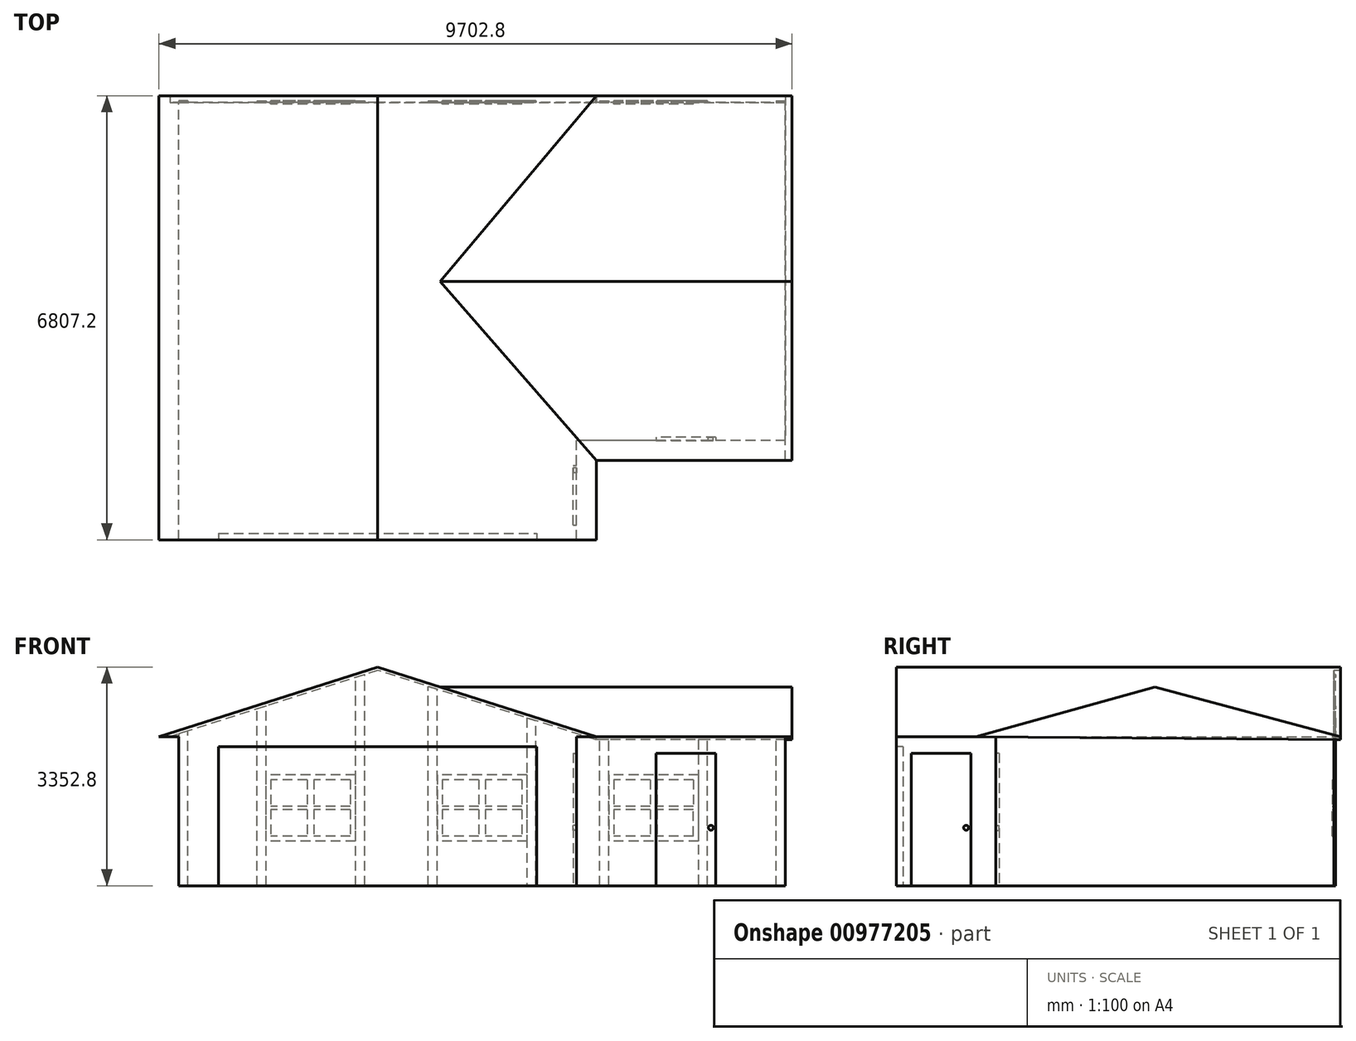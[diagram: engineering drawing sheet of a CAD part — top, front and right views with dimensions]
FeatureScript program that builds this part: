
annotation { "Feature Type Name" : "Feature", "Feature Type Description" : "" }
export const myFeature = defineFeature(function(context is Context, id is Id, definition is map)
    precondition{}
    {
        {
            var Q0;
            Q0=qCreatedBy(makeId("Front.planeOp"),FACE);
            var sketch = newSketch(context, id + "F0", { "sketchPlane" : qUnion([Q0])});
            skLineSegment(sketch, "E0", {"start": v(334.67, 1660.37) * mm, "end": v(-3018.13, 593.57) * mm});
            skLineSegment(sketch, "E1", {"start": v(-3018.13, 593.57) * mm, "end": v(-2713.33, 593.57) * mm});
            skLineSegment(sketch, "E2", {"start": v(-2713.33, 593.57) * mm, "end": v(-2713.33, -1692.43) * mm});
            skLineSegment(sketch, "E3", {"start": v(-2713.33, -1692.43) * mm, "end": v(3382.67, -1692.43) * mm});
            skLineSegment(sketch, "E4", {"start": v(3382.67, -1692.43) * mm, "end": v(3382.67, 593.57) * mm});
            skLineSegment(sketch, "E5", {"start": v(3382.67, 593.57) * mm, "end": v(3687.47, 593.57) * mm});
            skLineSegment(sketch, "E6", {"start": v(3687.47, 593.57) * mm, "end": v(334.67, 1660.37) * mm});
            skSolve(sketch);
        }
        {
            var Q0;
            Q0 = qSketchRegion(id + "F0", true);
            extrude(context, id + "F1", {"entities" : qUnion([Q0]), "depth" : 22 * 304.8 * mm, "offsetDistance" : 25.4 * mm});
        }
        {
            var Q0;
            Q0=makeQuery(id+"F1.opExtrude","CAP_FACE",FACE,{"disambiguationData":[OSD([sQuery(id+"F0.wireOp",EDGE,"E0"),sQuery(id+"F0.wireOp",EDGE,"E1"),sQuery(id+"F0.wireOp",EDGE,"E2"),sQuery(id+"F0.wireOp",EDGE,"E3"),sQuery(id+"F0.wireOp",EDGE,"E4"),sQuery(id+"F0.wireOp",EDGE,"E5"),sQuery(id+"F0.wireOp",EDGE,"E6")])],"isStart":false});
            var sketch = newSketch(context, id + "F2", { "sketchPlane" : qUnion([Q0])});
            skLineSegment(sketch, "E7.bottom", {"start": v(-2103.73, 441.17) * mm, "end": v(2773.07, 441.17) * mm});
            skLineSegment(sketch, "E7.top", {"start": v(-2103.73, -1692.43) * mm, "end": v(2773.07, -1692.43) * mm});
            skLineSegment(sketch, "E7.left", {"start": v(-2103.73, 441.17) * mm, "end": v(-2103.73, -1692.43) * mm});
            skLineSegment(sketch, "E7.right", {"start": v(2773.07, 441.17) * mm, "end": v(2773.07, -1692.43) * mm});
            skSolve(sketch);
        }
        {
            var Q0;
            Q0 = qSketchRegion(id + "F2", true);
            extrude(context, id + "F3", {"entities" : qUnion([Q0]), "operationType" : NewBodyOperationType.REMOVE, "oppositeDirection" : true, "depth" : 101.6 * mm, "offsetDistance" : 25.4 * mm});
        }
        {
            var Q0;
            Q0=makeQuery(id+"F1.opExtrude","SWEPT_FACE",FACE,{"disambiguationData":[OSD([sQuery(id+"F0.wireOp",EDGE,"E4")])]});
            var sketch = newSketch(context, id + "F4", { "sketchPlane" : qUnion([Q0])});
            skLineSegment(sketch, "E8.bottom", {"start": v(-6477, 339.57) * mm, "end": v(-5562.6, 339.57) * mm});
            skLineSegment(sketch, "E8.top", {"start": v(-6477, -1692.43) * mm, "end": v(-5562.6, -1692.43) * mm});
            skLineSegment(sketch, "E8.left", {"start": v(-6477, 339.57) * mm, "end": v(-6477, -1692.43) * mm});
            skLineSegment(sketch, "E8.right", {"start": v(-5562.6, 339.57) * mm, "end": v(-5562.6, -1692.43) * mm});
            skSolve(sketch);
        }
        {
            var Q0;
            Q0 = qSketchRegion(id + "F4", true);
            extrude(context, id + "F5", {"entities" : qUnion([Q0]), "operationType" : NewBodyOperationType.REMOVE, "oppositeDirection" : true, "depth" : 50.8 * mm, "offsetDistance" : 25.4 * mm});
        }
        {
            var Q0;
            Q0=makeQuery(id+"F1.opExtrude","SWEPT_FACE",FACE,{"disambiguationData":[OSD([sQuery(id+"F0.wireOp",EDGE,"E4")])]});
            var sketch = newSketch(context, id + "F6", { "sketchPlane" : qUnion([Q0])});
            skLineSegment(sketch, "E9", {"start": v(-5181.6, -1692.43) * mm, "end": v(-5181.6, 593.57) * mm});
            skLineSegment(sketch, "E10", {"start": v(-5181.6, 593.57) * mm, "end": v(-5486.4, 593.57) * mm});
            skLineSegment(sketch, "E11", {"start": v(-5486.4, 593.57) * mm, "end": v(-2743.2, 1355.57) * mm});
            skLineSegment(sketch, "E12", {"start": v(0, 593.57) * mm, "end": v(0, -1692.43) * mm});
            skLineSegment(sketch, "E13", {"start": v(0, -1692.43) * mm, "end": v(-5181.6, -1692.43) * mm});
            skLineSegment(sketch, "E14", {"start": v(-2743.2, 1355.57) * mm, "end": v(0, 593.57) * mm});
            skSolve(sketch);
        }
        {
            var Q0;
            Q0 = qSketchRegion(id + "F6", true);
            var Q1;
            Q1=makeQuery(id+"F1.opExtrude","SWEPT_FACE",FACE,{"disambiguationData":[OSD([sQuery(id+"F0.wireOp",EDGE,"E6")])]});
            extrude(context, id + "F7", {"entities" : qUnion([Q0]), "operationType" : NewBodyOperationType.ADD, "depth" : 3200.4 * mm, "offsetDistance" : 25.4 * mm, "hasSecondDirection" : true, "secondDirectionBound" : SecondDirectionBoundingType.UP_TO_NEXT, "secondDirectionOppositeDirection" : true, "secondDirectionDepth" : 25.4 * mm, "secondDirectionBoundEntityFace" : qUnion([Q1])});
        }
        {
            var Q0;
            Q0=makeQuery(id+"F7.opExtrude","SWEPT_FACE",FACE,{"disambiguationData":[OSD([sQuery(id+"F6.wireOp",EDGE,"E9")])]});
            var sketch = newSketch(context, id + "F8", { "sketchPlane" : qUnion([Q0])});
            skLineSegment(sketch, "E15.bottom", {"start": v(4601.87, 339.57) * mm, "end": v(5516.27, 339.57) * mm});
            skLineSegment(sketch, "E15.top", {"start": v(4601.87, -1692.43) * mm, "end": v(5516.27, -1692.43) * mm});
            skLineSegment(sketch, "E15.left", {"start": v(4601.87, 339.57) * mm, "end": v(4601.87, -1692.43) * mm});
            skLineSegment(sketch, "E15.right", {"start": v(5516.27, 339.57) * mm, "end": v(5516.27, -1692.43) * mm});
            skSolve(sketch);
        }
        {
            var Q0;
            Q0 = qSketchRegion(id + "F8", true);
            extrude(context, id + "F9", {"entities" : qUnion([Q0]), "operationType" : NewBodyOperationType.REMOVE, "oppositeDirection" : true, "depth" : 50.8 * mm, "offsetDistance" : 25.4 * mm});
        }
        {
            var Q0;
            Q0=makeQuery(id+"F7.boolean.opBoolean","MERGE",FACE,{"derivedFrom":[makeQuery(id+"F1.opExtrude","CAP_FACE",FACE,{"disambiguationData":[OSD([sQuery(id+"F0.wireOp",EDGE,"E0"),sQuery(id+"F0.wireOp",EDGE,"E1"),sQuery(id+"F0.wireOp",EDGE,"E2"),sQuery(id+"F0.wireOp",EDGE,"E3"),sQuery(id+"F0.wireOp",EDGE,"E4"),sQuery(id+"F0.wireOp",EDGE,"E5"),sQuery(id+"F0.wireOp",EDGE,"E6")])],"isStart":true}),makeQuery(id+"F7.opExtrude","SWEPT_FACE",FACE,{"disambiguationData":[OSD([sQuery(id+"F6.wireOp",EDGE,"E12")])]})]});
            var sketch = newSketch(context, id + "F10", { "sketchPlane" : qUnion([Q0])});
            skLineSegment(sketch, "E16.bottom", {"start": v(-5173.37, -66.83) * mm, "end": v(-4614.57, -66.83) * mm});
            skLineSegment(sketch, "E16.top", {"start": v(-5173.37, -930.43) * mm, "end": v(-4614.57, -930.43) * mm});
            skLineSegment(sketch, "E16.left", {"start": v(-5173.37, -66.83) * mm, "end": v(-5173.37, -473.23) * mm});
            skLineSegment(sketch, "E16.right", {"start": v(-4614.57, -66.83) * mm, "end": v(-4614.57, -473.23) * mm});
            skLineSegment(sketch, "E17.top", {"start": v(-4512.97, -930.43) * mm, "end": v(-3954.17, -930.43) * mm});
            skLineSegment(sketch, "E17.left", {"start": v(-4512.97, -66.83) * mm, "end": v(-4512.97, -473.23) * mm});
            skLineSegment(sketch, "E17.right", {"start": v(-3954.17, -66.83) * mm, "end": v(-3954.17, -473.23) * mm});
            skLineSegment(sketch, "E18.top", {"start": v(-2544.47, -930.43) * mm, "end": v(-1985.67, -930.43) * mm});
            skLineSegment(sketch, "E18.left", {"start": v(-2544.47, -66.83) * mm, "end": v(-2544.47, -473.23) * mm});
            skLineSegment(sketch, "E18.right", {"start": v(-1985.67, -66.83) * mm, "end": v(-1985.67, -473.23) * mm});
            skLineSegment(sketch, "E19.top", {"start": v(-1884.07, -930.43) * mm, "end": v(-1325.27, -930.43) * mm});
            skLineSegment(sketch, "E19.left", {"start": v(-1884.07, -66.83) * mm, "end": v(-1884.07, -473.23) * mm});
            skLineSegment(sketch, "E19.right", {"start": v(-1325.27, -66.83) * mm, "end": v(-1325.27, -473.23) * mm});
            skLineSegment(sketch, "E20.top", {"start": v(84.43, -930.43) * mm, "end": v(643.23, -930.43) * mm});
            skLineSegment(sketch, "E20.left", {"start": v(84.43, -66.83) * mm, "end": v(84.43, -473.23) * mm});
            skLineSegment(sketch, "E20.right", {"start": v(643.23, -66.83) * mm, "end": v(643.23, -473.23) * mm});
            skLineSegment(sketch, "E21.top", {"start": v(744.83, -930.43) * mm, "end": v(1303.63, -930.43) * mm});
            skLineSegment(sketch, "E21.left", {"start": v(744.83, -66.83) * mm, "end": v(744.83, -473.23) * mm});
            skLineSegment(sketch, "E21.right", {"start": v(1303.63, -66.83) * mm, "end": v(1303.63, -473.23) * mm});
            skLineSegment(sketch, "E22", {"start": v(-4512.97, -524.03) * mm, "end": v(-3954.17, -524.03) * mm});
            skLineSegment(sketch, "E23", {"start": v(-2544.47, -524.03) * mm, "end": v(-1985.67, -524.03) * mm});
            skLineSegment(sketch, "E24", {"start": v(-1884.07, -524.03) * mm, "end": v(-1325.27, -524.03) * mm});
            skLineSegment(sketch, "E25", {"start": v(84.43, -524.03) * mm, "end": v(643.23, -524.03) * mm});
            skLineSegment(sketch, "E26", {"start": v(744.83, -524.03) * mm, "end": v(1303.63, -524.03) * mm});
            skLineSegment(sketch, "E27", {"start": v(-5173.37, -473.23) * mm, "end": v(-4614.57, -473.23) * mm});
            skLineSegment(sketch, "E28", {"start": v(-4512.97, -473.23) * mm, "end": v(-3954.17, -473.23) * mm});
            skLineSegment(sketch, "E29", {"start": v(-2544.47, -473.23) * mm, "end": v(-1985.67, -473.23) * mm});
            skLineSegment(sketch, "E30", {"start": v(-1884.07, -473.23) * mm, "end": v(-1325.27, -473.23) * mm});
            skLineSegment(sketch, "E31", {"start": v(84.43, -473.23) * mm, "end": v(643.23, -473.23) * mm});
            skLineSegment(sketch, "E32", {"start": v(744.83, -473.23) * mm, "end": v(1303.63, -473.23) * mm});
            skLineSegment(sketch, "E33.trimOffspring", {"start": v(-3954.17, -524.03) * mm, "end": v(-3954.17, -930.43) * mm});
            skLineSegment(sketch, "E34.trimOffspring", {"start": v(-4614.57, -524.03) * mm, "end": v(-4614.57, -930.43) * mm});
            skLineSegment(sketch, "E35.trimOffspring", {"start": v(-4512.97, -524.03) * mm, "end": v(-4512.97, -930.43) * mm});
            skLineSegment(sketch, "E36.trimOffspring", {"start": v(-2544.47, -524.03) * mm, "end": v(-2544.47, -930.43) * mm});
            skLineSegment(sketch, "E37.trimOffspring", {"start": v(-1884.07, -524.03) * mm, "end": v(-1884.07, -930.43) * mm});
            skLineSegment(sketch, "E38.trimOffspring", {"start": v(-1325.27, -524.03) * mm, "end": v(-1325.27, -930.43) * mm});
            skLineSegment(sketch, "E39.trimOffspring", {"start": v(-1985.67, -524.03) * mm, "end": v(-1985.67, -930.43) * mm});
            skLineSegment(sketch, "E40.trimOffspring", {"start": v(84.43, -524.03) * mm, "end": v(84.43, -930.43) * mm});
            skLineSegment(sketch, "E41.trimOffspring", {"start": v(643.23, -524.03) * mm, "end": v(643.23, -930.43) * mm});
            skLineSegment(sketch, "E42.trimOffspring", {"start": v(744.83, -524.03) * mm, "end": v(744.83, -930.43) * mm});
            skLineSegment(sketch, "E43.trimOffspring", {"start": v(1303.63, -524.03) * mm, "end": v(1303.63, -930.43) * mm});
            skLineSegment(sketch, "E44", {"start": v(-5173.37, -930.43) * mm, "end": v(-5173.37, -524.03) * mm});
            skLineSegment(sketch, "E45", {"start": v(-5173.37, -524.03) * mm, "end": v(-4614.57, -524.03) * mm});
            skLineSegment(sketch, "E46", {"start": v(-4512.97, -66.83) * mm, "end": v(-3954.17, -66.83) * mm});
            skLineSegment(sketch, "E47.trimOffspring", {"start": v(-2544.47, -66.83) * mm, "end": v(-1985.67, -66.83) * mm});
            skLineSegment(sketch, "E48.trimOffspring", {"start": v(84.43, -66.83) * mm, "end": v(643.23, -66.83) * mm});
            skLineSegment(sketch, "E49.trimOffspring", {"start": v(744.83, -66.83) * mm, "end": v(1303.63, -66.83) * mm});
            skLineSegment(sketch, "E50.trimOffspring", {"start": v(-1884.07, -66.83) * mm, "end": v(-1325.27, -66.83) * mm});
            skSolve(sketch);
        }
        {
            var Q0;
            Q0 = qSketchRegion(id + "F10", true);
            extrude(context, id + "F11", {"entities" : qUnion([Q0]), "operationType" : NewBodyOperationType.REMOVE, "oppositeDirection" : true, "depth" : 25.4 * mm, "offsetDistance" : 25.4 * mm});
        }
        {
            var Q0;
            Q0=makeQuery(id+"F7.boolean.opBoolean","MERGE",FACE,{"derivedFrom":[makeQuery(id+"F1.opExtrude","CAP_FACE",FACE,{"disambiguationData":[OSD([sQuery(id+"F0.wireOp",EDGE,"E0"),sQuery(id+"F0.wireOp",EDGE,"E1"),sQuery(id+"F0.wireOp",EDGE,"E2"),sQuery(id+"F0.wireOp",EDGE,"E3"),sQuery(id+"F0.wireOp",EDGE,"E4"),sQuery(id+"F0.wireOp",EDGE,"E5"),sQuery(id+"F0.wireOp",EDGE,"E6")])],"isStart":true}),makeQuery(id+"F7.opExtrude","SWEPT_FACE",FACE,{"disambiguationData":[OSD([sQuery(id+"F6.wireOp",EDGE,"E12")])]})]});
            var sketch = newSketch(context, id + "F12", { "sketchPlane" : qUnion([Q0])});
            skLineSegment(sketch, "E51.bottom", {"start": v(-5249.57, 9.37) * mm, "end": v(-3877.97, 9.37) * mm});
            skLineSegment(sketch, "E51.top", {"start": v(-5249.57, -1006.63) * mm, "end": v(-3877.97, -1006.63) * mm});
            skLineSegment(sketch, "E51.left", {"start": v(-5249.57, 9.37) * mm, "end": v(-5249.57, -1006.63) * mm});
            skLineSegment(sketch, "E51.right", {"start": v(-3877.97, 9.37) * mm, "end": v(-3877.97, -1006.63) * mm});
            skLineSegment(sketch, "E52.bottom", {"start": v(-2620.67, 9.37) * mm, "end": v(-1249.07, 9.37) * mm});
            skLineSegment(sketch, "E52.top", {"start": v(-2620.67, -1006.63) * mm, "end": v(-1249.07, -1006.63) * mm});
            skLineSegment(sketch, "E52.left", {"start": v(-2620.67, 9.37) * mm, "end": v(-2620.67, -1006.63) * mm});
            skLineSegment(sketch, "E52.right", {"start": v(-1249.07, 9.37) * mm, "end": v(-1249.07, -1006.63) * mm});
            skLineSegment(sketch, "E53.bottom", {"start": v(8.23, 9.37) * mm, "end": v(1379.83, 9.37) * mm});
            skLineSegment(sketch, "E53.top", {"start": v(8.23, -1006.63) * mm, "end": v(1379.83, -1006.63) * mm});
            skLineSegment(sketch, "E53.left", {"start": v(8.23, 9.37) * mm, "end": v(8.23, -1006.63) * mm});
            skLineSegment(sketch, "E53.right", {"start": v(1379.83, 9.37) * mm, "end": v(1379.83, -1006.63) * mm});
            skLineSegment(sketch, "E54.bottom", {"start": v(-5173.37, -66.83) * mm, "end": v(-4614.57, -66.83) * mm});
            skLineSegment(sketch, "E54.top", {"start": v(-5173.37, -473.23) * mm, "end": v(-4614.57, -473.23) * mm});
            skLineSegment(sketch, "E54.left", {"start": v(-5173.37, -66.83) * mm, "end": v(-5173.37, -473.23) * mm});
            skLineSegment(sketch, "E54.right", {"start": v(-4614.57, -66.83) * mm, "end": v(-4614.57, -473.23) * mm});
            skLineSegment(sketch, "E55.bottom", {"start": v(-4512.97, -66.83) * mm, "end": v(-3954.17, -66.83) * mm});
            skLineSegment(sketch, "E55.top", {"start": v(-4512.97, -473.23) * mm, "end": v(-3954.17, -473.23) * mm});
            skLineSegment(sketch, "E55.left", {"start": v(-4512.97, -66.83) * mm, "end": v(-4512.97, -473.23) * mm});
            skLineSegment(sketch, "E55.right", {"start": v(-3954.17, -66.83) * mm, "end": v(-3954.17, -473.23) * mm});
            skLineSegment(sketch, "E56.bottom", {"start": v(-4512.97, -524.03) * mm, "end": v(-3954.17, -524.03) * mm});
            skLineSegment(sketch, "E56.top", {"start": v(-4512.97, -930.43) * mm, "end": v(-3954.17, -930.43) * mm});
            skLineSegment(sketch, "E56.left", {"start": v(-4512.97, -524.03) * mm, "end": v(-4512.97, -930.43) * mm});
            skLineSegment(sketch, "E56.right", {"start": v(-3954.17, -524.03) * mm, "end": v(-3954.17, -930.43) * mm});
            skLineSegment(sketch, "E57.bottom", {"start": v(-5173.37, -524.03) * mm, "end": v(-4614.57, -524.03) * mm});
            skLineSegment(sketch, "E57.top", {"start": v(-5173.37, -930.43) * mm, "end": v(-4614.57, -930.43) * mm});
            skLineSegment(sketch, "E57.left", {"start": v(-5173.37, -524.03) * mm, "end": v(-5173.37, -930.43) * mm});
            skLineSegment(sketch, "E57.right", {"start": v(-4614.57, -524.03) * mm, "end": v(-4614.57, -930.43) * mm});
            skLineSegment(sketch, "E58.bottom", {"start": v(-2544.47, -66.83) * mm, "end": v(-1985.67, -66.83) * mm});
            skLineSegment(sketch, "E58.top", {"start": v(-2544.47, -473.23) * mm, "end": v(-1985.67, -473.23) * mm});
            skLineSegment(sketch, "E58.left", {"start": v(-2544.47, -66.83) * mm, "end": v(-2544.47, -473.23) * mm});
            skLineSegment(sketch, "E58.right", {"start": v(-1985.67, -66.83) * mm, "end": v(-1985.67, -473.23) * mm});
            skLineSegment(sketch, "E59.bottom", {"start": v(-1884.07, -66.83) * mm, "end": v(-1325.27, -66.83) * mm});
            skLineSegment(sketch, "E59.top", {"start": v(-1884.07, -473.23) * mm, "end": v(-1325.27, -473.23) * mm});
            skLineSegment(sketch, "E59.left", {"start": v(-1884.07, -66.83) * mm, "end": v(-1884.07, -473.23) * mm});
            skLineSegment(sketch, "E59.right", {"start": v(-1325.27, -66.83) * mm, "end": v(-1325.27, -473.23) * mm});
            skLineSegment(sketch, "E60.bottom", {"start": v(84.43, -66.83) * mm, "end": v(643.23, -66.83) * mm});
            skLineSegment(sketch, "E60.top", {"start": v(84.43, -473.23) * mm, "end": v(643.23, -473.23) * mm});
            skLineSegment(sketch, "E60.left", {"start": v(84.43, -66.83) * mm, "end": v(84.43, -473.23) * mm});
            skLineSegment(sketch, "E60.right", {"start": v(643.23, -66.83) * mm, "end": v(643.23, -473.23) * mm});
            skLineSegment(sketch, "E61.bottom", {"start": v(744.83, -66.83) * mm, "end": v(1303.63, -66.83) * mm});
            skLineSegment(sketch, "E61.top", {"start": v(744.83, -473.23) * mm, "end": v(1303.63, -473.23) * mm});
            skLineSegment(sketch, "E61.left", {"start": v(744.83, -66.83) * mm, "end": v(744.83, -473.23) * mm});
            skLineSegment(sketch, "E61.right", {"start": v(1303.63, -66.83) * mm, "end": v(1303.63, -473.23) * mm});
            skLineSegment(sketch, "E62.bottom", {"start": v(744.83, -524.03) * mm, "end": v(1303.63, -524.03) * mm});
            skLineSegment(sketch, "E62.top", {"start": v(744.83, -930.43) * mm, "end": v(1303.63, -930.43) * mm});
            skLineSegment(sketch, "E62.left", {"start": v(744.83, -524.03) * mm, "end": v(744.83, -930.43) * mm});
            skLineSegment(sketch, "E62.right", {"start": v(1303.63, -524.03) * mm, "end": v(1303.63, -930.43) * mm});
            skLineSegment(sketch, "E63.bottom", {"start": v(-1884.07, -524.03) * mm, "end": v(-1325.27, -524.03) * mm});
            skLineSegment(sketch, "E63.top", {"start": v(-1884.07, -930.43) * mm, "end": v(-1325.27, -930.43) * mm});
            skLineSegment(sketch, "E63.left", {"start": v(-1884.07, -524.03) * mm, "end": v(-1884.07, -930.43) * mm});
            skLineSegment(sketch, "E63.right", {"start": v(-1325.27, -524.03) * mm, "end": v(-1325.27, -930.43) * mm});
            skLineSegment(sketch, "E64.bottom", {"start": v(-2544.47, -524.03) * mm, "end": v(-1985.67, -524.03) * mm});
            skLineSegment(sketch, "E64.top", {"start": v(-2544.47, -930.43) * mm, "end": v(-1985.67, -930.43) * mm});
            skLineSegment(sketch, "E64.left", {"start": v(-2544.47, -524.03) * mm, "end": v(-2544.47, -930.43) * mm});
            skLineSegment(sketch, "E64.right", {"start": v(-1985.67, -524.03) * mm, "end": v(-1985.67, -930.43) * mm});
            skLineSegment(sketch, "E65.bottom", {"start": v(84.43, -524.03) * mm, "end": v(643.23, -524.03) * mm});
            skLineSegment(sketch, "E65.top", {"start": v(84.43, -930.43) * mm, "end": v(643.23, -930.43) * mm});
            skLineSegment(sketch, "E65.left", {"start": v(84.43, -524.03) * mm, "end": v(84.43, -930.43) * mm});
            skLineSegment(sketch, "E65.right", {"start": v(643.23, -524.03) * mm, "end": v(643.23, -930.43) * mm});
            skSolve(sketch);
        }
        {
            var Q0;
            Q0=makeQuery(id+"F7.boolean.opBoolean","MERGE",FACE,{"derivedFrom":[makeQuery(id+"F1.opExtrude","CAP_FACE",FACE,{"disambiguationData":[OSD([sQuery(id+"F0.wireOp",EDGE,"E0"),sQuery(id+"F0.wireOp",EDGE,"E1"),sQuery(id+"F0.wireOp",EDGE,"E2"),sQuery(id+"F0.wireOp",EDGE,"E3"),sQuery(id+"F0.wireOp",EDGE,"E4"),sQuery(id+"F0.wireOp",EDGE,"E5"),sQuery(id+"F0.wireOp",EDGE,"E6")])],"isStart":true}),makeQuery(id+"F7.opExtrude","SWEPT_FACE",FACE,{"disambiguationData":[OSD([sQuery(id+"F6.wireOp",EDGE,"E12")])]})]});
            var sketch = newSketch(context, id + "F13", { "sketchPlane" : qUnion([Q0])});
            skLineSegment(sketch, "E66.bottom", {"start": v(-5389.27, 593.57) * mm, "end": v(-5249.57, 593.57) * mm});
            skLineSegment(sketch, "E66.top", {"start": v(-5389.27, -1692.43) * mm, "end": v(-5249.57, -1692.43) * mm});
            skLineSegment(sketch, "E66.left", {"start": v(-5389.27, 593.57) * mm, "end": v(-5389.27, -1692.43) * mm});
            skLineSegment(sketch, "E66.right", {"start": v(-5249.57, 593.57) * mm, "end": v(-5249.57, -1692.43) * mm});
            skLineSegment(sketch, "E67.bottom", {"start": v(-3738.27, -1692.43) * mm, "end": v(-3877.97, -1692.43) * mm});
            skLineSegment(sketch, "E67.top", {"start": v(-3738.27, 593.57) * mm, "end": v(-3877.97, 593.57) * mm});
            skLineSegment(sketch, "E67.left", {"start": v(-3738.27, -1692.43) * mm, "end": v(-3738.27, 593.57) * mm});
            skLineSegment(sketch, "E67.right", {"start": v(-3877.97, -1692.43) * mm, "end": v(-3877.97, 593.57) * mm});
            skLineSegment(sketch, "E68.bottom", {"start": v(-2620.67, -1692.43) * mm, "end": v(-2760.37, -1692.43) * mm});
            skLineSegment(sketch, "E68.top", {"start": v(-2620.67, 593.57) * mm, "end": v(-2760.37, 593.57) * mm});
            skLineSegment(sketch, "E68.left", {"start": v(-2620.67, -1692.43) * mm, "end": v(-2620.67, 593.57) * mm});
            skLineSegment(sketch, "E68.right", {"start": v(-2760.37, -1692.43) * mm, "end": v(-2760.37, 593.57) * mm});
            skLineSegment(sketch, "E69.bottom", {"start": v(-1109.37, -1692.43) * mm, "end": v(-1249.07, -1692.43) * mm});
            skLineSegment(sketch, "E69.top", {"start": v(-1109.37, 593.57) * mm, "end": v(-1249.07, 593.57) * mm});
            skLineSegment(sketch, "E69.left", {"start": v(-1109.37, -1692.43) * mm, "end": v(-1109.37, 593.57) * mm});
            skLineSegment(sketch, "E69.right", {"start": v(-1249.07, -1692.43) * mm, "end": v(-1249.07, 593.57) * mm});
            skLineSegment(sketch, "E70.bottom", {"start": v(-131.47, -1692.43) * mm, "end": v(8.23, -1692.43) * mm});
            skLineSegment(sketch, "E70.top", {"start": v(-131.47, 593.57) * mm, "end": v(8.23, 593.57) * mm});
            skLineSegment(sketch, "E70.left", {"start": v(-131.47, -1692.43) * mm, "end": v(-131.47, 593.57) * mm});
            skLineSegment(sketch, "E70.right", {"start": v(8.23, -1692.43) * mm, "end": v(8.23, 593.57) * mm});
            skLineSegment(sketch, "E71.bottom", {"start": v(1522.36, -1692.43) * mm, "end": v(1382.66, -1692.43) * mm});
            skLineSegment(sketch, "E71.top", {"start": v(1522.36, 593.57) * mm, "end": v(1382.66, 593.57) * mm});
            skLineSegment(sketch, "E71.left", {"start": v(1522.36, -1692.43) * mm, "end": v(1522.36, 593.57) * mm});
            skLineSegment(sketch, "E71.right", {"start": v(1382.66, -1692.43) * mm, "end": v(1382.66, 593.57) * mm});
            skLineSegment(sketch, "E72.bottom", {"start": v(2713.33, -1692.43) * mm, "end": v(2573.63, -1692.43) * mm});
            skLineSegment(sketch, "E72.top", {"start": v(2713.33, 593.57) * mm, "end": v(2573.63, 593.57) * mm});
            skLineSegment(sketch, "E72.left", {"start": v(2713.33, -1692.43) * mm, "end": v(2713.33, 593.57) * mm});
            skLineSegment(sketch, "E72.right", {"start": v(2573.63, -1692.43) * mm, "end": v(2573.63, 593.57) * mm});
            skLineSegment(sketch, "E73.bottom", {"start": v(-6583.07, -1692.43) * mm, "end": v(-6443.37, -1692.43) * mm});
            skLineSegment(sketch, "E73.top", {"start": v(-6583.07, 593.57) * mm, "end": v(-6443.37, 593.57) * mm});
            skLineSegment(sketch, "E73.left", {"start": v(-6583.07, -1692.43) * mm, "end": v(-6583.07, 593.57) * mm});
            skLineSegment(sketch, "E73.right", {"start": v(-6443.37, -1692.43) * mm, "end": v(-6443.37, 593.57) * mm});
            skSolve(sketch);
        }
        {
            var Q0;
            Q0 = qSketchRegion(id + "F12", true);
            extrude(context, id + "F14", {"entities" : qUnion([Q0]), "operationType" : NewBodyOperationType.ADD, "depth" : 25.4 * mm, "offsetDistance" : 25.4 * mm});
        }
        {
            var Q0;
            {var subQ16=sQuery(id+"F13.wireOp",EDGE,"E67.left");Q0=makeQuery(id+"F13.imprint","IMPRINT",FACE,{"disambiguationData":[TD([[makeQuery(id+"F13.imprint","IMPRINT",EDGE,{"derivedFrom":subQ16}),-1.0]])]});}
            var sketch = newSketch(context, id + "F15", { "sketchPlane" : qUnion([Q0])});
            skLineSegment(sketch, "E74", {"start": v(-334.67, 1660.37) * mm, "end": v(-3687.47, 593.57) * mm});
            skLineSegment(sketch, "E75", {"start": v(-3687.47, 593.57) * mm, "end": v(-3672.07, 545.16) * mm});
            skLineSegment(sketch, "E76", {"start": v(-3672.07, 545.16) * mm, "end": v(-334.67, 1607.06) * mm});
            skLineSegment(sketch, "E77", {"start": v(-334.67, 1607.06) * mm, "end": v(2850.58, 593.57) * mm});
            skLineSegment(sketch, "E78", {"start": v(2850.58, 593.57) * mm, "end": v(3018.13, 593.57) * mm});
            skLineSegment(sketch, "E79", {"start": v(3018.13, 593.57) * mm, "end": v(-334.67, 1660.37) * mm});
            skSolve(sketch);
        }
        {
            var Q0;
            Q0 = qSketchRegion(id + "F15", true);
            extrude(context, id + "F16", {"entities" : qUnion([Q0]), "operationType" : NewBodyOperationType.ADD, "depth" : 101.6 * mm, "offsetDistance" : 25.4 * mm});
        }
        {
            var Q0;
            {var subQ0=sQuery(id+"F6.wireOp",EDGE,"E12");var subQ1=sQuery(id+"F6.wireOp",EDGE,"E11");var subQ2=sQuery(id+"F6.wireOp",EDGE,"E10");var subQ3=sQuery(id+"F6.wireOp",EDGE,"E9");var subQ4=sQuery(id+"F6.wireOp",EDGE,"E13");var subQ5=sQuery(id+"F6.wireOp",EDGE,"E14");Q0=makeQuery(id+"F7.opExtrude","CAP_FACE",FACE,{"disambiguationData":[OSD([subQ3,subQ2,subQ1,subQ0,subQ4,subQ5]),topologyDisambiguationEdgeConnected([makeQuery(id+"F6.imprint","IMPRINT",EDGE,{"derivedFrom":subQ3})])],"isStart":false});}
            var sketch = newSketch(context, id + "F17", { "sketchPlane" : qUnion([Q0])});
            skLineSegment(sketch, "E80", {"start": v(-2743.2, 1355.57) * mm, "end": v(101.6, 593.57) * mm});
            skLineSegment(sketch, "E81", {"start": v(101.6, 593.57) * mm, "end": v(101.6, 545.05) * mm});
            skLineSegment(sketch, "E82", {"start": v(101.6, 545.05) * mm, "end": v(-2743.2, 545.05) * mm});
            skLineSegment(sketch, "E83", {"start": v(-2743.2, 545.05) * mm, "end": v(-2743.2, 1355.57) * mm});
            skSolve(sketch);
        }
        {
            var Q0;
            Q0 = qSketchRegion(id + "F17", true);
            var Q1;
            Q1=makeQuery(id+"F16.boolean.opBoolean","MERGE",FACE,{"derivedFrom":[makeQuery(id+"F1.opExtrude","SWEPT_FACE",FACE,{"disambiguationData":[OSD([sQuery(id+"F0.wireOp",EDGE,"E6")])]}),makeQuery(id+"F16.opExtrude","SWEPT_FACE",FACE,{"disambiguationData":[OSD([sQuery(id+"F15.wireOp",EDGE,"E74")])]})]});
            var Q2;
            Q2=makeQuery(id+"F1.opExtrude","SWEPT_BODY",BODY,{"disambiguationData":[OSD([sQuery(id+"F0.wireOp",EDGE,"E0"),sQuery(id+"F0.wireOp",EDGE,"E1"),sQuery(id+"F0.wireOp",EDGE,"E2"),sQuery(id+"F0.wireOp",EDGE,"E3"),sQuery(id+"F0.wireOp",EDGE,"E4"),sQuery(id+"F0.wireOp",EDGE,"E5"),sQuery(id+"F0.wireOp",EDGE,"E6")])]});
            extrude(context, id + "F18", {"entities" : qUnion([Q0]), "operationType" : NewBodyOperationType.ADD, "endBound" : BoundingType.UP_TO_SURFACE, "oppositeDirection" : true, "depth" : 25.4 * mm, "endBoundEntityFace" : qUnion([Q1]), "endBoundEntityBody" : qUnion([Q2]), "offsetDistance" : 25.4 * mm});
        }
        {
            var Q0;
            Q0=makeQuery(id+"F18.opExtrude","SWEPT_FACE",FACE,{"disambiguationData":[OSD([sQuery(id+"F17.wireOp",EDGE,"E81")])]});
            var sketch = newSketch(context, id + "F19", { "sketchPlane" : qUnion([Q0])});
            skLineSegment(sketch, "E84", {"start": v(-3839.95, 545.05) * mm, "end": v(-3672.67, 545.05) * mm});
            skLineSegment(sketch, "E85", {"start": v(-3672.67, 545.05) * mm, "end": v(-3687.47, 593.57) * mm});
            skLineSegment(sketch, "E86", {"start": v(-3687.47, 593.57) * mm, "end": v(-3839.95, 545.05) * mm});
            skSolve(sketch);
        }
        {
            var Q0;
            Q0 = qSketchRegion(id + "F19", true);
            var Q1;
            Q1=makeQuery(id+"F7.boolean.opBoolean","MERGE",FACE,{"derivedFrom":[makeQuery(id+"F1.opExtrude","CAP_FACE",FACE,{"disambiguationData":[OSD([sQuery(id+"F0.wireOp",EDGE,"E0"),sQuery(id+"F0.wireOp",EDGE,"E1"),sQuery(id+"F0.wireOp",EDGE,"E2"),sQuery(id+"F0.wireOp",EDGE,"E3"),sQuery(id+"F0.wireOp",EDGE,"E4"),sQuery(id+"F0.wireOp",EDGE,"E5"),sQuery(id+"F0.wireOp",EDGE,"E6")])],"isStart":true}),makeQuery(id+"F7.opExtrude","SWEPT_FACE",FACE,{"disambiguationData":[OSD([sQuery(id+"F6.wireOp",EDGE,"E12")])]})]});
            extrude(context, id + "F20", {"entities" : qUnion([Q0]), "operationType" : NewBodyOperationType.ADD, "endBound" : BoundingType.UP_TO_SURFACE, "oppositeDirection" : true, "depth" : 25.4 * mm, "endBoundEntityFace" : qUnion([Q1]), "offsetDistance" : 25.4 * mm});
        }
        {
            var Q0;
            Q0=makeQuery(id+"F7.boolean.opBoolean","MERGE",FACE,{"derivedFrom":[makeQuery(id+"F1.opExtrude","CAP_FACE",FACE,{"disambiguationData":[OSD([sQuery(id+"F0.wireOp",EDGE,"E0"),sQuery(id+"F0.wireOp",EDGE,"E1"),sQuery(id+"F0.wireOp",EDGE,"E2"),sQuery(id+"F0.wireOp",EDGE,"E3"),sQuery(id+"F0.wireOp",EDGE,"E4"),sQuery(id+"F0.wireOp",EDGE,"E5"),sQuery(id+"F0.wireOp",EDGE,"E6")])],"isStart":true}),makeQuery(id+"F7.opExtrude","SWEPT_FACE",FACE,{"disambiguationData":[OSD([sQuery(id+"F6.wireOp",EDGE,"E12")])]})]});
            var sketch = newSketch(context, id + "F21", { "sketchPlane" : qUnion([Q0])});
            skLineSegment(sketch, "E87.bottom", {"start": v(-6583.07, -1692.43) * mm, "end": v(-6443.37, -1692.43) * mm});
            skLineSegment(sketch, "E87.top", {"start": v(-6583.07, 545.05) * mm, "end": v(-6443.37, 545.05) * mm});
            skLineSegment(sketch, "E87.left", {"start": v(-6583.07, -1692.43) * mm, "end": v(-6583.07, 545.05) * mm});
            skLineSegment(sketch, "E87.right", {"start": v(-6443.37, -1692.43) * mm, "end": v(-6443.37, 545.05) * mm});
            skLineSegment(sketch, "E88.bottom", {"start": v(-5249.57, -1692.43) * mm, "end": v(-5389.27, -1692.43) * mm});
            skLineSegment(sketch, "E88.top", {"start": v(-5249.57, 545.05) * mm, "end": v(-5389.27, 545.05) * mm});
            skLineSegment(sketch, "E88.left", {"start": v(-5249.57, -1692.43) * mm, "end": v(-5249.57, 545.05) * mm});
            skLineSegment(sketch, "E88.right", {"start": v(-5389.27, -1692.43) * mm, "end": v(-5389.27, 545.05) * mm});
            skLineSegment(sketch, "E89.bottom", {"start": v(-3877.97, -1692.43) * mm, "end": v(-3738.27, -1692.43) * mm});
            skLineSegment(sketch, "E89.top", {"start": v(-3877.97, 545.05) * mm, "end": v(-3738.27, 545.05) * mm});
            skLineSegment(sketch, "E89.left", {"start": v(-3877.97, -1692.43) * mm, "end": v(-3877.97, 545.05) * mm});
            skLineSegment(sketch, "E89.right", {"start": v(-3738.27, -1692.43) * mm, "end": v(-3738.27, 545.05) * mm});
            skLineSegment(sketch, "E90.bottom", {"start": v(-2620.67, -1692.43) * mm, "end": v(-2760.37, -1692.43) * mm});
            skLineSegment(sketch, "E90.left", {"start": v(-2620.67, -1692.43) * mm, "end": v(-2620.67, 879.7) * mm});
            skLineSegment(sketch, "E90.right", {"start": v(-2760.37, -1692.43) * mm, "end": v(-2760.37, 835.24) * mm});
            skLineSegment(sketch, "E91.bottom", {"start": v(7.5, -1692.43) * mm, "end": v(-132.2, -1692.43) * mm});
            skLineSegment(sketch, "E91.left", {"start": v(7.5, -1692.43) * mm, "end": v(7.5, 1498.18) * mm});
            skLineSegment(sketch, "E91.right", {"start": v(-132.2, -1692.43) * mm, "end": v(-132.2, 1542.63) * mm});
            skLineSegment(sketch, "E92.bottom", {"start": v(-1109.37, -1692.43) * mm, "end": v(-1249.07, -1692.43) * mm});
            skLineSegment(sketch, "E92.left", {"start": v(-1109.37, -1692.43) * mm, "end": v(-1109.37, 1360.56) * mm});
            skLineSegment(sketch, "E92.right", {"start": v(-1249.07, -1692.43) * mm, "end": v(-1249.07, 1316.11) * mm});
            skLineSegment(sketch, "E93.bottom", {"start": v(1518.46, -1692.43) * mm, "end": v(1378.76, -1692.43) * mm});
            skLineSegment(sketch, "E93.left", {"start": v(1518.46, -1692.43) * mm, "end": v(1518.46, 1017.43) * mm});
            skLineSegment(sketch, "E93.right", {"start": v(1378.76, -1692.43) * mm, "end": v(1378.76, 1061.88) * mm});
            skLineSegment(sketch, "E94.bottom", {"start": v(2713.33, -1692.43) * mm, "end": v(2573.63, -1692.43) * mm});
            skLineSegment(sketch, "E94.left", {"start": v(2713.33, -1692.43) * mm, "end": v(2713.33, 637.24) * mm});
            skLineSegment(sketch, "E94.right", {"start": v(2573.63, -1692.43) * mm, "end": v(2573.63, 681.69) * mm});
            skLineSegment(sketch, "E95", {"start": v(-2760.37, 835.24) * mm, "end": v(-2620.67, 879.7) * mm});
            skLineSegment(sketch, "E96", {"start": v(-132.2, 1542.63) * mm, "end": v(7.5, 1498.18) * mm});
            skPoint(sketch, "E97.orphan", {"position": v(-1249.07, 1607.06) * mm});
            skLineSegment(sketch, "E98.trimOffspring", {"start": v(-1249.07, 1316.11) * mm, "end": v(-1109.37, 1360.56) * mm});
            skLineSegment(sketch, "E99.trimOffspring", {"start": v(1378.76, 1061.88) * mm, "end": v(1518.46, 1017.43) * mm});
            skLineSegment(sketch, "E100.trimOffspring", {"start": v(2573.63, 681.69) * mm, "end": v(2713.33, 637.24) * mm});
            skSolve(sketch);
        }
        {
            var Q0;
            Q0 = qSketchRegion(id + "F21", true);
            extrude(context, id + "F22", {"entities" : qUnion([Q0]), "depth" : 25.4 * mm, "offsetDistance" : 25.4 * mm});
        }
        {
            var Q0;
            Q0=makeQuery(id+"F5.boolean.opBoolean","COPY",FACE,{"derivedFrom":makeQuery(id+"F5.opExtrude","CAP_FACE",FACE,{"disambiguationData":[OSD([sQuery(id+"F4.wireOp",EDGE,"E8.bottom"),sQuery(id+"F4.wireOp",EDGE,"E8.top"),sQuery(id+"F4.wireOp",EDGE,"E8.left"),sQuery(id+"F4.wireOp",EDGE,"E8.right")])],"isStart":false})});
            var sketch = newSketch(context, id + "F23", { "sketchPlane" : qUnion([Q0])});
            skCircle(sketch, "E101", {"center": v(-5638.8, -803.43) * mm, "radius": 38.1 * mm});
            skSolve(sketch);
        }
        {
            var Q0;
            Q0=makeQuery(id+"F9.boolean.opBoolean","COPY",FACE,{"derivedFrom":makeQuery(id+"F9.opExtrude","CAP_FACE",FACE,{"disambiguationData":[OSD([sQuery(id+"F8.wireOp",EDGE,"E15.bottom"),sQuery(id+"F8.wireOp",EDGE,"E15.top"),sQuery(id+"F8.wireOp",EDGE,"E15.left"),sQuery(id+"F8.wireOp",EDGE,"E15.right")])],"isStart":false})});
            var sketch = newSketch(context, id + "F24", { "sketchPlane" : qUnion([Q0])});
            skCircle(sketch, "E102", {"center": v(5440.07, -803.43) * mm, "radius": 38.1 * mm});
            skSolve(sketch);
        }
        {
            var Q0;
            Q0 = qSketchRegion(id + "F23", true);
            extrude(context, id + "F25", {"entities" : qUnion([Q0]), "operationType" : NewBodyOperationType.ADD, "depth" : 50.8 * mm, "offsetDistance" : 25.4 * mm});
        }
        {
            var Q0;
            Q0 = qSketchRegion(id + "F24", true);
            extrude(context, id + "F26", {"entities" : qUnion([Q0]), "operationType" : NewBodyOperationType.ADD, "depth" : 50.8 * mm, "offsetDistance" : 25.4 * mm});
        }
        {
            var Q0;
            {var subQ0=sQuery(id+"F6.wireOp",EDGE,"E12");var subQ1=sQuery(id+"F6.wireOp",EDGE,"E11");var subQ2=sQuery(id+"F6.wireOp",EDGE,"E10");var subQ3=sQuery(id+"F6.wireOp",EDGE,"E9");var subQ4=sQuery(id+"F6.wireOp",EDGE,"E13");var subQ5=sQuery(id+"F6.wireOp",EDGE,"E14");Q0=makeQuery(id+"F18.boolean.opBoolean","MERGE",FACE,{"derivedFrom":[makeQuery(id+"F7.opExtrude","CAP_FACE",FACE,{"disambiguationData":[OSD([subQ3,subQ2,subQ1,subQ0,subQ4,subQ5]),topologyDisambiguationEdgeConnected([makeQuery(id+"F6.imprint","IMPRINT",EDGE,{"derivedFrom":subQ3})])],"isStart":false}),makeQuery(id+"F18.opExtrude","CAP_FACE",FACE,{"disambiguationData":[OSD([sQuery(id+"F17.wireOp",EDGE,"E80"),sQuery(id+"F17.wireOp",EDGE,"E81"),sQuery(id+"F17.wireOp",EDGE,"E82"),sQuery(id+"F17.wireOp",EDGE,"E83")])],"isStart":true})]});}
            var sketch = newSketch(context, id + "F27", { "sketchPlane" : qUnion([Q0])});
            skLineSegment(sketch, "E103", {"start": v(-5486.4, 593.57) * mm, "end": v(-2743.2, 1355.57) * mm});
            skLineSegment(sketch, "E104", {"start": v(-2743.2, 1355.57) * mm, "end": v(101.6, 593.57) * mm});
            skLineSegment(sketch, "E105", {"start": v(101.6, 593.57) * mm, "end": v(101.6, 545.05) * mm});
            skLineSegment(sketch, "E106", {"start": v(101.6, 545.05) * mm, "end": v(-5486.4, 593.57) * mm});
            skSolve(sketch);
        }
        {
            var Q0;
            Q0 = qSketchRegion(id + "F27", true);
            extrude(context, id + "F28", {"entities" : qUnion([Q0]), "operationType" : NewBodyOperationType.ADD, "depth" : 101.6 * mm, "offsetDistance" : 25.4 * mm});
        }
    });
